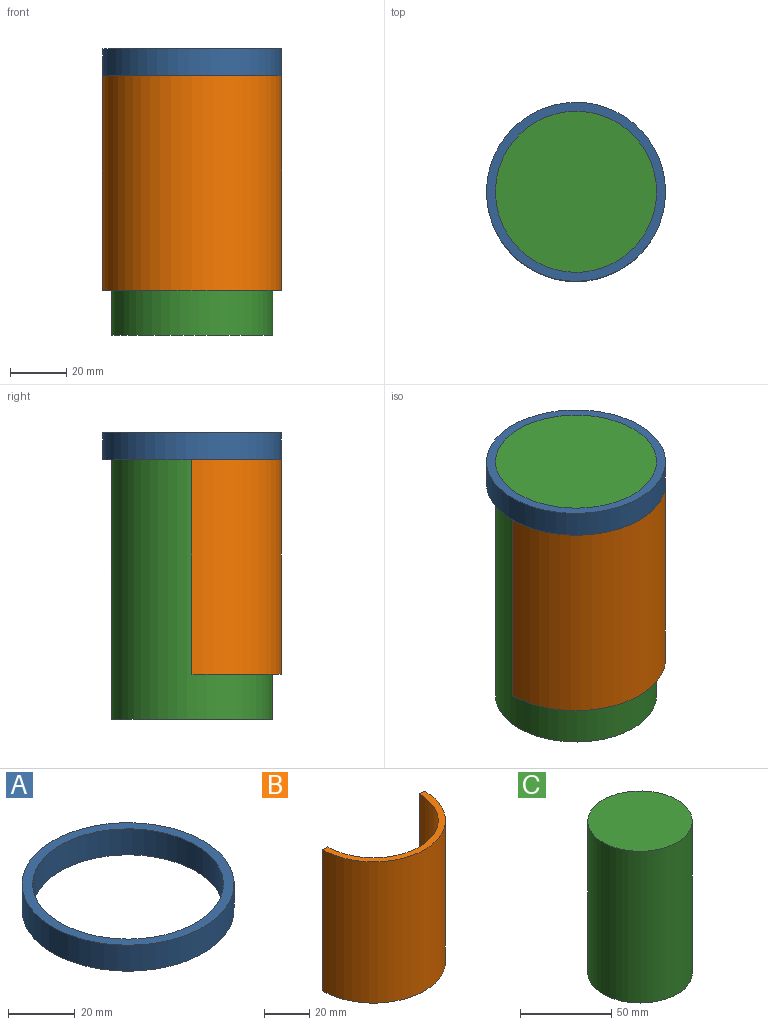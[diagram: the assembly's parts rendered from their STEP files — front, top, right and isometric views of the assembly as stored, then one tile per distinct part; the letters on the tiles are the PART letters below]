
ASSEMBLY  parts=3 mates=3
PART A: 4 faces, bbox 63.5x63.5x9.5 mm
  f0: cylinder r=28.57mm len=57.15mm, axis (0,0,-1), area 1710.1mm2, adj f2,f3
  f1: cylinder r=31.75mm len=63.5mm, axis (0,0,-1), area 1900.2mm2, adj f2,f3
  f2: plane 63.5x63.5mm, normal (0,0,1), area 601.7mm2, adj f0,f1
  f3: plane 63.5x63.5mm, normal (0,0,-1), area 601.7mm2, adj f0,f1
PART B: 6 faces, bbox 63.5x31.8x76.2 mm
  f0: cylinder r=28.57mm len=76.2mm, axis (0,0,-1), area 6840.6mm2, adj f1,f3,f4,f5
  f1: plane 76.2x3.18mm, normal (0,1,0), area 241.9mm2, adj f0,f2,f4,f5
  f2: cylinder r=31.75mm len=76.2mm, axis (0,0,-1), area 7600.6mm2, adj f1,f3,f4,f5
  f3: plane 76.2x3.18mm, normal (0,1,0), area 241.9mm2, adj f0,f2,f4,f5
  f4: plane 63.5x31.75mm, normal (0,0,1), area 300.9mm2, adj f0,f1,f2,f3
  f5: plane 63.5x31.75mm, normal (0,0,-1), area 300.9mm2, adj f0,f1,f2,f3
PART C: 3 faces, bbox 57.2x57.2x101.6 mm
  f0: cylinder r=28.57mm len=101.6mm, axis (0,0,-1), area 18241.5mm2, adj f1,f2
  f1: plane 57.15x57.15mm, normal (0,0,1), area 2565.2mm2, adj f0
  f2: plane 57.15x57.15mm, normal (0,0,-1), area 2565.2mm2, adj f0
PLACE A t=(83.81,11.94,-9.52)mm
PLACE B t=(83.81,11.94,-85.72)mm
PLACE C t=(83.81,11.94,-50.8)mm
MATE slider C.f0 <-> A.f0  axis (0,0,1) through (83.81,11.94,0)mm
MATE cylindrical A.f0 <-> C.f0  axis (0,0,1) through (83.81,11.94,0)mm
MATE cylindrical C.f0 <-> B.f0  axis (0,0,-1) through (83.81,11.94,-101.6)mm
